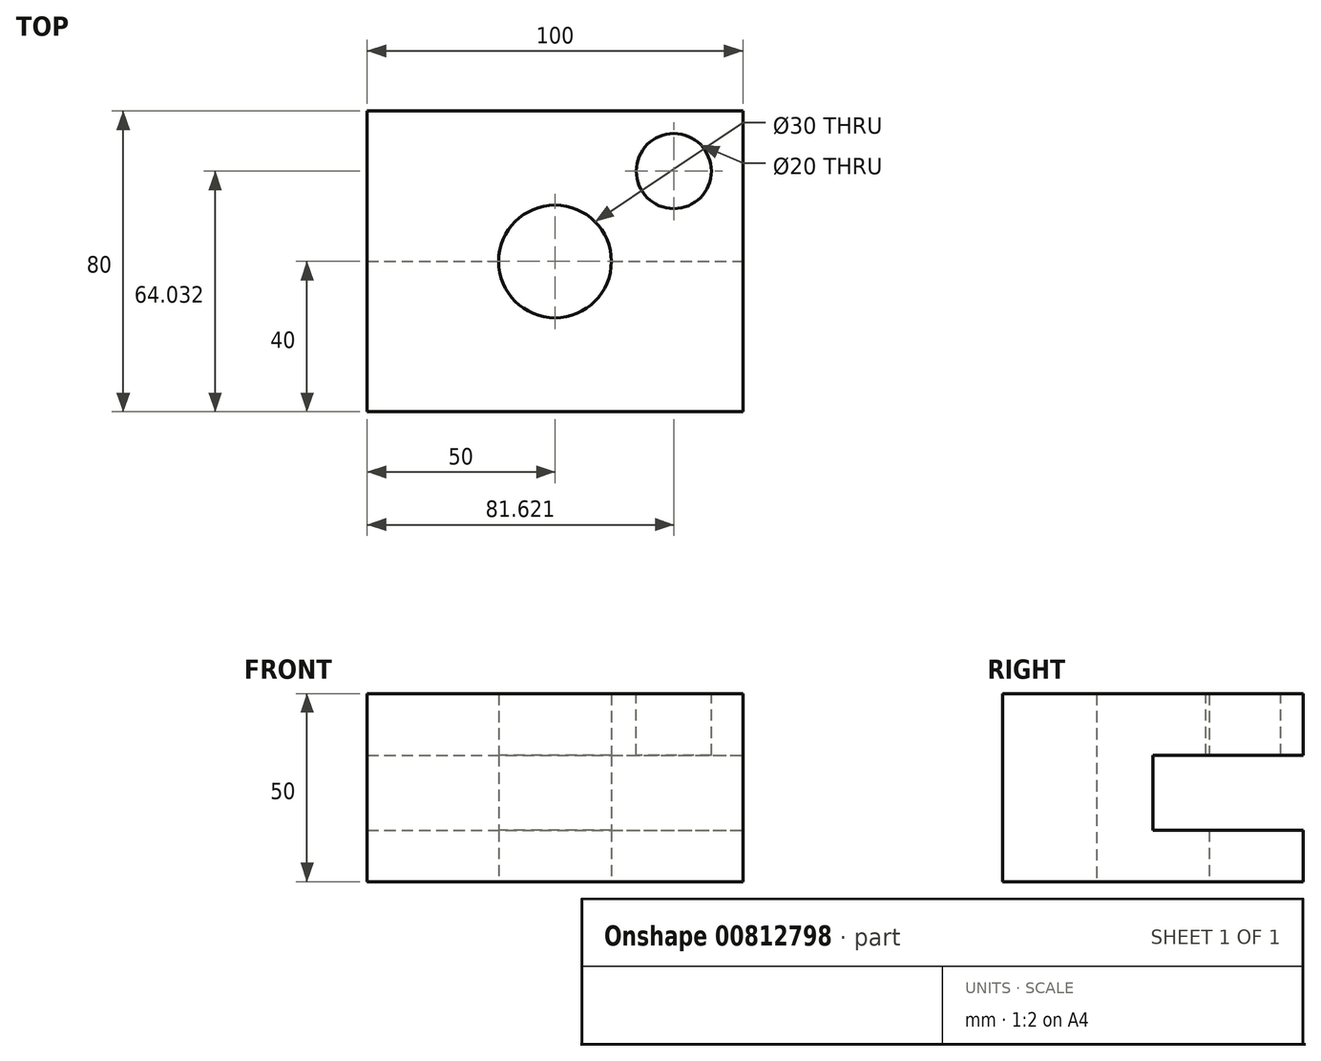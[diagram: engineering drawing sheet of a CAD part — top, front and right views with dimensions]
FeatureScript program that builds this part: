
annotation { "Feature Type Name" : "Feature", "Feature Type Description" : "" }
export const myFeature = defineFeature(function(context is Context, id is Id, definition is map)
    precondition{}
    {
        {
            var Q0;
            Q0=qCreatedBy(makeId("Top.planeOp"),FACE);
            var sketch = newSketch(context, id + "F0", { "sketchPlane" : qUnion([Q0])});
            skLineSegment(sketch, "E0.bottom", {"start": v(-50, 40) * mm, "end": v(50, 40) * mm});
            skLineSegment(sketch, "E0.top", {"start": v(-50, -40) * mm, "end": v(50, -40) * mm});
            skLineSegment(sketch, "E0.left", {"start": v(-50, 40) * mm, "end": v(-50, -40) * mm});
            skLineSegment(sketch, "E0.right", {"start": v(50, 40) * mm, "end": v(50, -40) * mm});
            skCircle(sketch, "E1", {"center": v(0, 0) * mm, "radius": 15 * mm});
            skSolve(sketch);
        }
        {
            var Q0;
            Q0=makeQuery(id+"F0.imprint","IMPRINT",FACE,{"disambiguationData":[TD([[makeQuery(id+"F0.imprint","IMPRINT",EDGE,{"derivedFrom":sQuery(id+"F0.wireOp",EDGE,"E0.bottom")}),-1.0]])]});
            extrude(context, id + "F1", {"entities" : qUnion([Q0]), "depth" : 50 * mm, "offsetDistance" : 25 * mm});
        }
        {
            var Q0;
            Q0=qCreatedBy(makeId("Front.planeOp"),FACE);
            cPlane(context, id + "F2", {"entities" : qUnion([Q0]), "cplaneType" : CPlaneType.OFFSET, "offset" : 40 * mm, "oppositeDirection" : true, "width" : 150 * mm, "height" : 150 * mm});
        }
        {
            var Q0;
            Q0=qCreatedBy(id+"F2.planeOp",FACE);
            var sketch = newSketch(context, id + "F3", { "sketchPlane" : qUnion([Q0])});
            skLineSegment(sketch, "E2.bottom", {"start": v(-60.3, 13.63) * mm, "end": v(62.26, 13.63) * mm});
            skLineSegment(sketch, "E2.top", {"start": v(-60.3, 33.63) * mm, "end": v(62.26, 33.63) * mm});
            skLineSegment(sketch, "E2.left", {"start": v(-60.3, 13.63) * mm, "end": v(-60.3, 33.63) * mm});
            skLineSegment(sketch, "E2.right", {"start": v(62.26, 13.63) * mm, "end": v(62.26, 33.63) * mm});
            skSolve(sketch);
        }
        {
            var Q0;
            Q0=makeQuery(id+"F3.imprint","IMPRINT",FACE,{"disambiguationData":[TD([[makeQuery(id+"F3.imprint","IMPRINT",EDGE,{"derivedFrom":sQuery(id+"F3.wireOp",EDGE,"E2.bottom")}),1.0]])]});
            extrude(context, id + "F4", {"entities" : qUnion([Q0]), "operationType" : NewBodyOperationType.REMOVE, "depth" : 40 * mm, "offsetDistance" : 25 * mm});
        }
        {
            var Q0;
            Q0=makeQuery(id+"F1.opExtrude","CAP_FACE",FACE,{"disambiguationData":[OSD([sQuery(id+"F0.wireOp",EDGE,"E0.bottom"),sQuery(id+"F0.wireOp",EDGE,"E0.top"),sQuery(id+"F0.wireOp",EDGE,"E0.left"),sQuery(id+"F0.wireOp",EDGE,"E0.right"),sQuery(id+"F0.wireOp",EDGE,"E1")])],"isStart":false});
            var sketch = newSketch(context, id + "F5", { "sketchPlane" : qUnion([Q0])});
            skCircle(sketch, "E3", {"center": v(31.62, 24.03) * mm, "radius": 10 * mm});
            skSolve(sketch);
        }
        {
            var Q0;
            Q0=makeQuery(id+"F5.imprint","IMPRINT",FACE,{"disambiguationData":[TD([[makeQuery(id+"F5.imprint","IMPRINT",EDGE,{"derivedFrom":sQuery(id+"F5.wireOp",EDGE,"E3")}),1.0]])]});
            extrude(context, id + "F6", {"entities" : qUnion([Q0]), "operationType" : NewBodyOperationType.REMOVE, "endBound" : BoundingType.UP_TO_NEXT, "oppositeDirection" : true, "depth" : 25 * mm, "offsetDistance" : 25 * mm});
        }
    });
